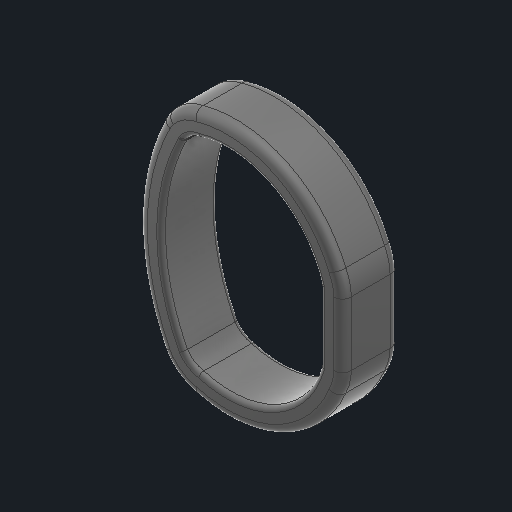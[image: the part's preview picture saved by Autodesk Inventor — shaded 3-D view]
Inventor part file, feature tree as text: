
AUTODESK INVENTOR PART (.ipt)
format: ipt  version: 2024 (Build 280153000, 153)  size: 492,032 bytes
history: native  units: in
note: dims shown in document units (in); Inventor stores cm internally (conversion verified against a paired STEP export)
features: fillet x3, extrude x1, sketch x1
ambient origin geometry x8: Origin, YZ Plane, XZ Plane, XY Plane, X Axis, Y Axis, Z Axis, Center Point
bodies: Solid1 (feature_tree)
feature tree (5):
  extrude  "Extrusion1"  Depth=0.0078in
  fillet  "Fillet1"  Radius=0.25in
  fillet  "Fillet2"  Radius=0.125in
  fillet  "Fillet3"  Radius=0.013in
  sketch  "Sketch1"  dims[d2=0.159in d3=0.1875in d7=0.25in d8=0.125in d9=0.013in d10=0.1681in d11=0.0625in d13=0.0375in d14=0.04in d15=0.04in d16=0.1in d17=0.0in d18=0.0156in d19=0.0078in d20=0.0078in d21=0.0in d22=0.0in]
